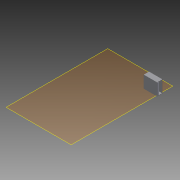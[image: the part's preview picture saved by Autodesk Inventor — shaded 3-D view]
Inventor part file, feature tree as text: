
AUTODESK INVENTOR PART (.ipt)
format: ipt  version: 2013 SP2 (Build 170200200, 200)  size: 103,424 bytes
history: native  units: mm
features: extrude x3, sketch x3, plane x1
ambient origin geometry x8: Origin, YZ Plane, XZ Plane, XY Plane, X Axis, Y Axis, Z Axis, Center Point
bodies: Solid1 (feature_tree)
feature tree (7):
  plane  "Work Plane1"
  extrude  "Extrusion1"  Depth=5.7mm
  extrude  "Extrusion2"  Depth=0.4mm
  extrude  "Extrusion3"  Depth=0.2mm
  sketch  "Sketch1"  dims[d0=14.5mm d2=5.7mm]
  sketch  "Sketch2"  dims[d3=13.2mm d4=0.0mm d5=0.4mm]
  sketch  "Sketch3"  dims[d6=13.0mm d7=0.0mm d8=0.2mm d9=0.2mm d10=0.2mm d11=1.4mm d12=13.0mm d13=0.0mm]
